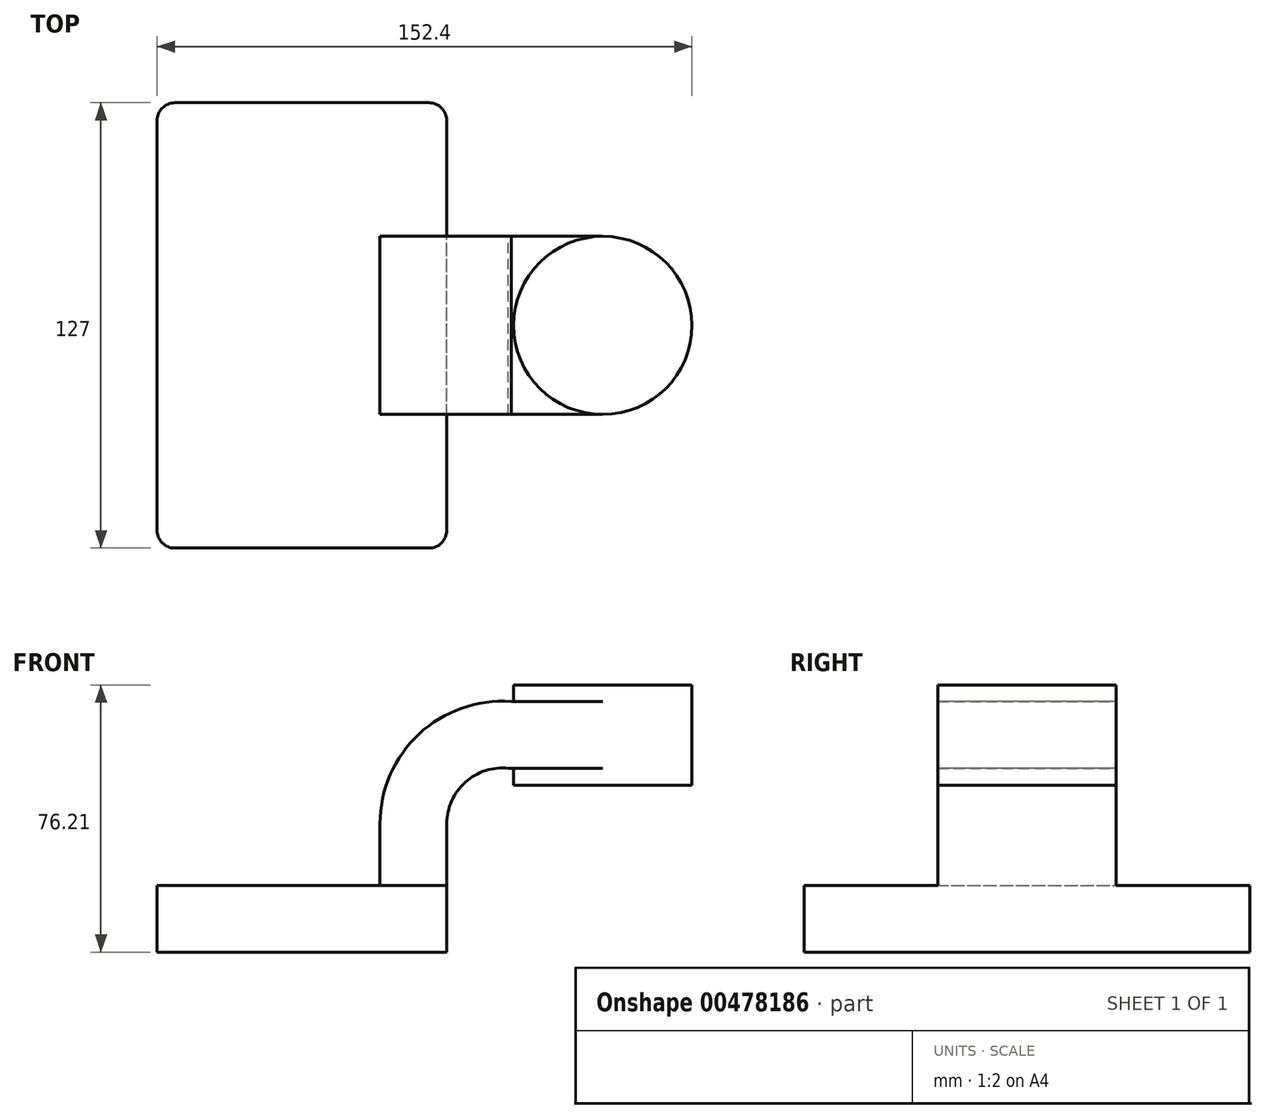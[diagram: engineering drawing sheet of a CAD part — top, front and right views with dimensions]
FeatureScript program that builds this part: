
annotation { "Feature Type Name" : "Feature", "Feature Type Description" : "" }
export const myFeature = defineFeature(function(context is Context, id is Id, definition is map)
    precondition{}
    {
        {
            var Q0;
            Q0=qCreatedBy(makeId("Front.planeOp"),FACE);
            var sketch = newSketch(context, id + "F0", { "sketchPlane" : qUnion([Q0])});
            skLineSegment(sketch, "E0.bottom", {"start": v(41.28, -9.52) * mm, "end": v(-41.27, -9.52) * mm});
            skLineSegment(sketch, "E0.top", {"start": v(41.27, 9.53) * mm, "end": v(-41.28, 9.53) * mm});
            skLineSegment(sketch, "E0.left", {"start": v(41.28, -9.52) * mm, "end": v(41.28, 9.53) * mm});
            skLineSegment(sketch, "E0.right", {"start": v(-41.27, -9.52) * mm, "end": v(-41.28, 9.53) * mm});
            skPoint(sketch, "E0.middle", {"position": v(0, 0) * mm});
            skLineSegment(sketch, "E1.bottom", {"start": v(111.12, 38.1) * mm, "end": v(60.32, 38.1) * mm});
            skLineSegment(sketch, "E1.top", {"start": v(111.12, 66.68) * mm, "end": v(60.32, 66.68) * mm});
            skLineSegment(sketch, "E1.left", {"start": v(111.12, 38.1) * mm, "end": v(111.12, 66.68) * mm});
            skLineSegment(sketch, "E1.right", {"start": v(60.32, 38.1) * mm, "end": v(60.32, 66.67) * mm});
            skPoint(sketch, "E1.middle", {"position": v(85.72, 52.39) * mm});
            skLineSegment(sketch, "E2", {"start": v(41.27, 9.53) * mm, "end": v(41.27, 27.1) * mm});
            skArc(sketch, "E3", {"start": v(41.28, 27.1) * mm, "mid": v(46.53, 38.9) * mm, "end": v(58.82, 42.89) * mm});
            skLineSegment(sketch, "E4", {"start": v(58.82, 42.89) * mm, "end": v(85.72, 42.89) * mm});
            skLineSegment(sketch, "E5.0", {"start": v(59.62, 61.94) * mm, "end": v(85.72, 61.94) * mm});
            skArc(sketch, "E5.1", {"start": v(22.23, 27.1) * mm, "mid": v(33.34, 52.66) * mm, "end": v(59.62, 61.94) * mm});
            skLineSegment(sketch, "E5.2", {"start": v(22.23, 9.53) * mm, "end": v(22.23, 27.1) * mm});
            skLineSegment(sketch, "E6", {"start": v(85.72, 66.68) * mm, "end": v(85.72, 38.1) * mm});
            skFitSpline(sketch, "E7", {"points": [v(59.62, 61.94) * mm, v(-41.28, 9.53) * mm], "startDerivative": vector(-115.74, 9.7) * mm, "endDerivative": vector(-85.45, -122.87) * mm});
            skSolve(sketch);
        }
        {
            var Q0;
            Q0=makeQuery(id+"F0.imprint","IMPRINT",FACE,{"disambiguationData":[TD([[makeQuery(id+"F0.imprint","IMPRINT",EDGE,{"derivedFrom":sQuery(id+"F0.wireOp",EDGE,"E0.bottom")}),-1.0]])]});
            extrude(context, id + "F1", {"entities" : qUnion([Q0]), "endBound" : BoundingType.SYMMETRIC, "depth" : 127 * mm});
        }
        {
            var Q0;
            {var subQ1=sQuery(id+"F0.wireOp",EDGE,"E2");Q0=makeQuery(id+"F0.imprint","IMPRINT",FACE,{"disambiguationData":[TD([[makeQuery(id+"F0.imprint","IMPRINT",EDGE,{"derivedFrom":subQ1}),1.0]])]});}
            var Q1;
            {var subQ0=sQuery(id+"F0.wireOp",EDGE,"E4");var subQ1=sQuery(id+"F0.wireOp",EDGE,"E1.right");var subQ2=makeQuery(id+"F0.imprint","INTERSECT",VERTEX,{"derivedFrom":[subQ1,subQ0]});Q1=makeQuery(id+"F0.imprint","IMPRINT",FACE,{"disambiguationData":[TD([[makeQuery(id+"F0.imprint","IMPRINT",EDGE,{"disambiguationData":[TD([[subQ2,-1.0]])],"derivedFrom":subQ1}),-1.0]])]});}
            extrude(context, id + "F2", {"entities" : qUnion([Q0, Q1]), "operationType" : NewBodyOperationType.ADD, "endBound" : BoundingType.SYMMETRIC, "depth" : 50.8 * mm});
        }
        {
            var Q0;
            Q0=makeQuery(id+"F0.imprint","IMPRINT",FACE,{"disambiguationData":[TD([[makeQuery(id+"F0.imprint","IMPRINT",EDGE,{"derivedFrom":sQuery(id+"F0.wireOp",EDGE,"E5.1")}),1.0]])]});
            extrude(context, id + "F3", {"entities" : qUnion([Q0]), "operationType" : NewBodyOperationType.ADD, "endBound" : BoundingType.SYMMETRIC, "depth" : 1 / 50.8 * mm});
        }
        {
            var Q0;
            {var subQ4=sQuery(id+"F0.wireOp",EDGE,"E1.left");Q0=makeQuery(id+"F0.imprint","IMPRINT",FACE,{"disambiguationData":[TD([[makeQuery(id+"F0.imprint","IMPRINT",EDGE,{"derivedFrom":subQ4}),1.0]])]});}
            var Q1;
            Q1=sQuery(id+"F0.wireOp",EDGE,"E6");
            revolve(context, id + "F4", {"operationType" : NewBodyOperationType.ADD, "entities" : qUnion([Q0]), "axis" : qUnion([Q1]), "revolveType" : RevolveType.FULL});
        }
        {
            var Q0;
            Q0=makeQuery(id+"F1.opExtrude","CAP_EDGE",EDGE,{"disambiguationData":[OSD([sQuery(id+"F0.wireOp",EDGE,"E0.left")])],"isStart":false});
            var Q1;
            Q1=makeQuery(id+"F1.opExtrude","CAP_EDGE",EDGE,{"disambiguationData":[OSD([sQuery(id+"F0.wireOp",EDGE,"E0.right")])],"isStart":false});
            var Q2;
            Q2=makeQuery(id+"F1.opExtrude","CAP_EDGE",EDGE,{"disambiguationData":[OSD([sQuery(id+"F0.wireOp",EDGE,"E0.left")])],"isStart":true});
            var Q3;
            Q3=makeQuery(id+"F1.opExtrude","CAP_EDGE",EDGE,{"disambiguationData":[OSD([sQuery(id+"F0.wireOp",EDGE,"E0.right")])],"isStart":true});
            fillet(context, id + "F5", {"entities" : qUnion([Q0, Q1, Q2, Q3]), "radius" : 5.08 * mm, "tangentPropagation" : true, "allowEdgeOverflow" : false});
        }
    });
